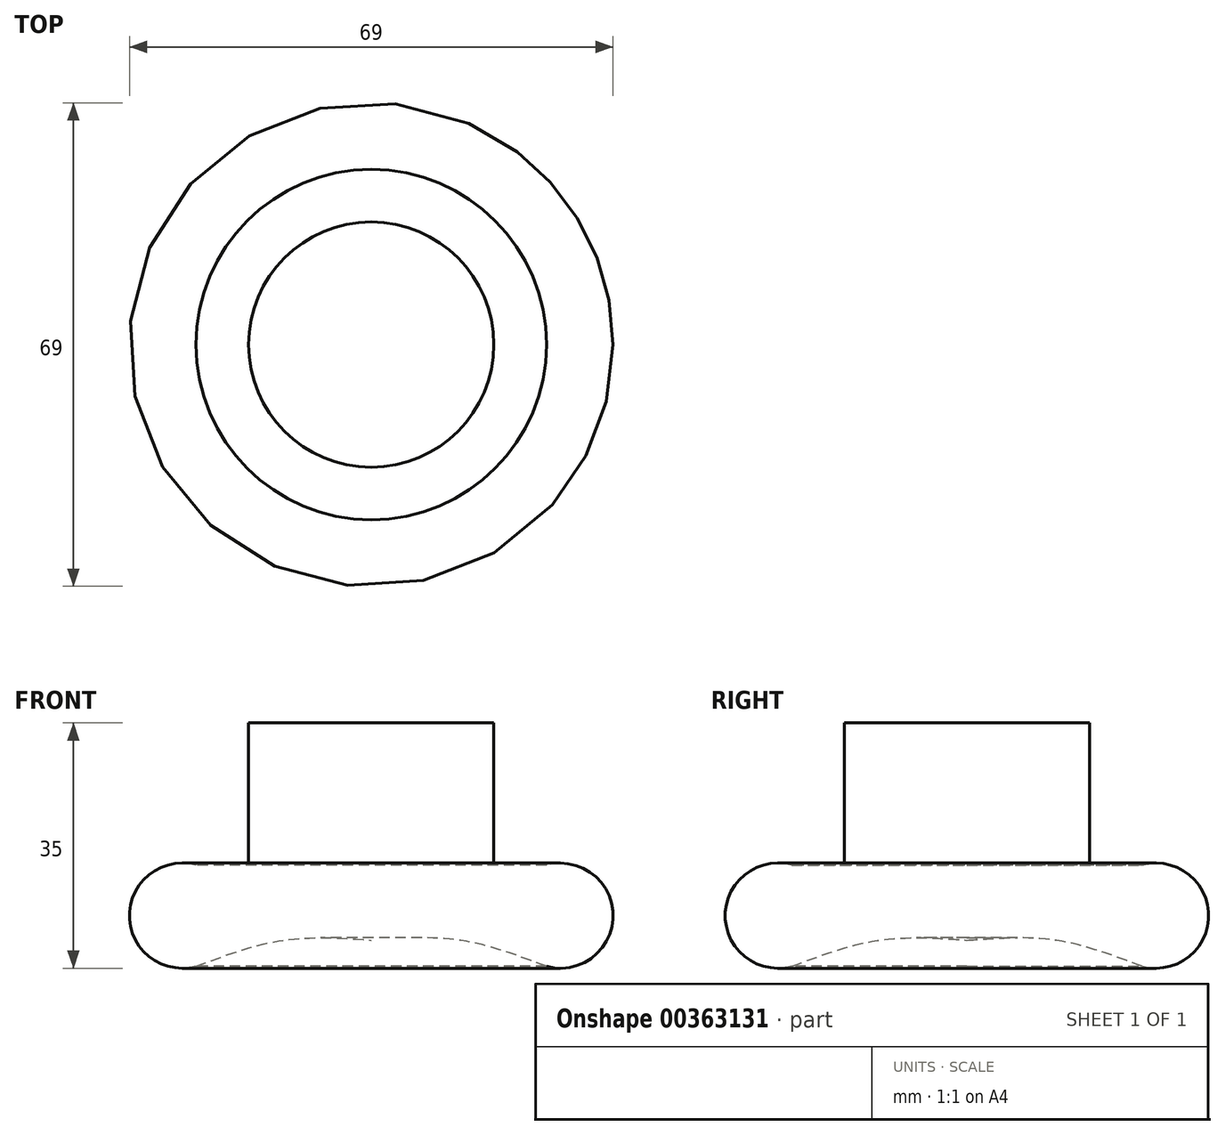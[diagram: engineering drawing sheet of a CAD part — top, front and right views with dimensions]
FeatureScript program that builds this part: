
annotation { "Feature Type Name" : "Feature", "Feature Type Description" : "" }
export const myFeature = defineFeature(function(context is Context, id is Id, definition is map)
    precondition{}
    {
        {
            var Q0;
            Q0=qCreatedBy(makeId("Front.planeOp"),FACE);
            var sketch = newSketch(context, id + "F0", { "sketchPlane" : qUnion([Q0])});
            skLineSegment(sketch, "E0", {"start": v(16.92, -1.63) * mm, "end": v(16.92, 1.87) * mm});
            skLineSegment(sketch, "E1", {"start": v(-8.08, -5.63) * mm, "end": v(-10.08, -5.63) * mm});
            skLineSegment(sketch, "E2", {"start": v(-8.08, 9.37) * mm, "end": v(-10.08, 9.37) * mm});
            skLineSegment(sketch, "E3", {"start": v(-8.08, 9.37) * mm, "end": v(-8.08, 9.1) * mm});
            skLineSegment(sketch, "E4", {"start": v(-8.08, 1.87) * mm, "end": v(-10.08, 1.87) * mm});
            skArc(sketch, "E5", {"start": v(-8.08, 9.1) * mm, "mid": v(-17.58, 1.87) * mm, "end": v(-8.08, -5.36) * mm});
            skPoint(sketch, "E6.start.orphan", {"position": v(-18.08, 9.37) * mm});
            skPoint(sketch, "E7.orphan", {"position": v(-18.08, -5.63) * mm});
            skLineSegment(sketch, "E8.trimOffspring", {"start": v(-8.08, -5.36) * mm, "end": v(-8.08, -5.63) * mm});
            skFitSpline(sketch, "E9", {"points": [v(-8.08, -5.36) * mm, v(4.42, -1.63) * mm, v(16.92, -1.63) * mm], "startDerivative": vector(24.6, 9.24) * mm, "endDerivative": vector(25.4, -1.82) * mm});
            skPoint(sketch, "E10.orphan", {"position": v(16.92, 9.37) * mm});
            skLineSegment(sketch, "E11", {"start": v(-8.08, 9.37) * mm, "end": v(16.92, 9.37) * mm});
            skLineSegment(sketch, "E12", {"start": v(16.92, -1.63) * mm, "end": v(16.92, 9.37) * mm});
            skPoint(sketch, "E13.orphan", {"position": v(16.92, -5.63) * mm});
            skLineSegment(sketch, "E14", {"start": v(16.92, 29.01) * mm, "end": v(16.92, -15.4) * mm});
            skSolve(sketch);
        }
        {
            var Q0;
            {var subQ4=sQuery(id+"F0.wireOp",EDGE,"E3");Q0=makeQuery(id+"F0.imprint","IMPRINT",FACE,{"disambiguationData":[TD([[makeQuery(id+"F0.imprint","IMPRINT",EDGE,{"derivedFrom":subQ4}),1.0]])]});}
            var Q1;
            Q1=sQuery(id+"F0.wireOp",EDGE,"E14");
            revolve(context, id + "F1", {"entities" : qUnion([Q0]), "axis" : qUnion([Q1]), "revolveType" : RevolveType.FULL});
        }
        {
            var Q0;
            Q0=makeQuery(id+"F1.opRevolve","SWEPT_FACE",FACE,{"disambiguationData":[OSD([sQuery(id+"F0.wireOp",EDGE,"E11")])]});
            var sketch = newSketch(context, id + "F2", { "sketchPlane" : qUnion([Q0])});
            skPoint(sketch, "E15", {"position": v(16.92, 0) * mm});
            skCircle(sketch, "E16", {"center": v(16.92, 0) * mm, "radius": 17.5 * mm});
            skSolve(sketch);
        }
        {
            var Q0;
            Q0=makeQuery(id+"F2.imprint","IMPRINT",FACE,{"disambiguationData":[TD([[makeQuery(id+"F2.imprint","IMPRINT",EDGE,{"derivedFrom":sQuery(id+"F2.wireOp",EDGE,"E16")}),1.0]])]});
            extrude(context, id + "F3", {"entities" : qUnion([Q0]), "operationType" : NewBodyOperationType.ADD, "depth" : 20 * mm});
        }
    });
